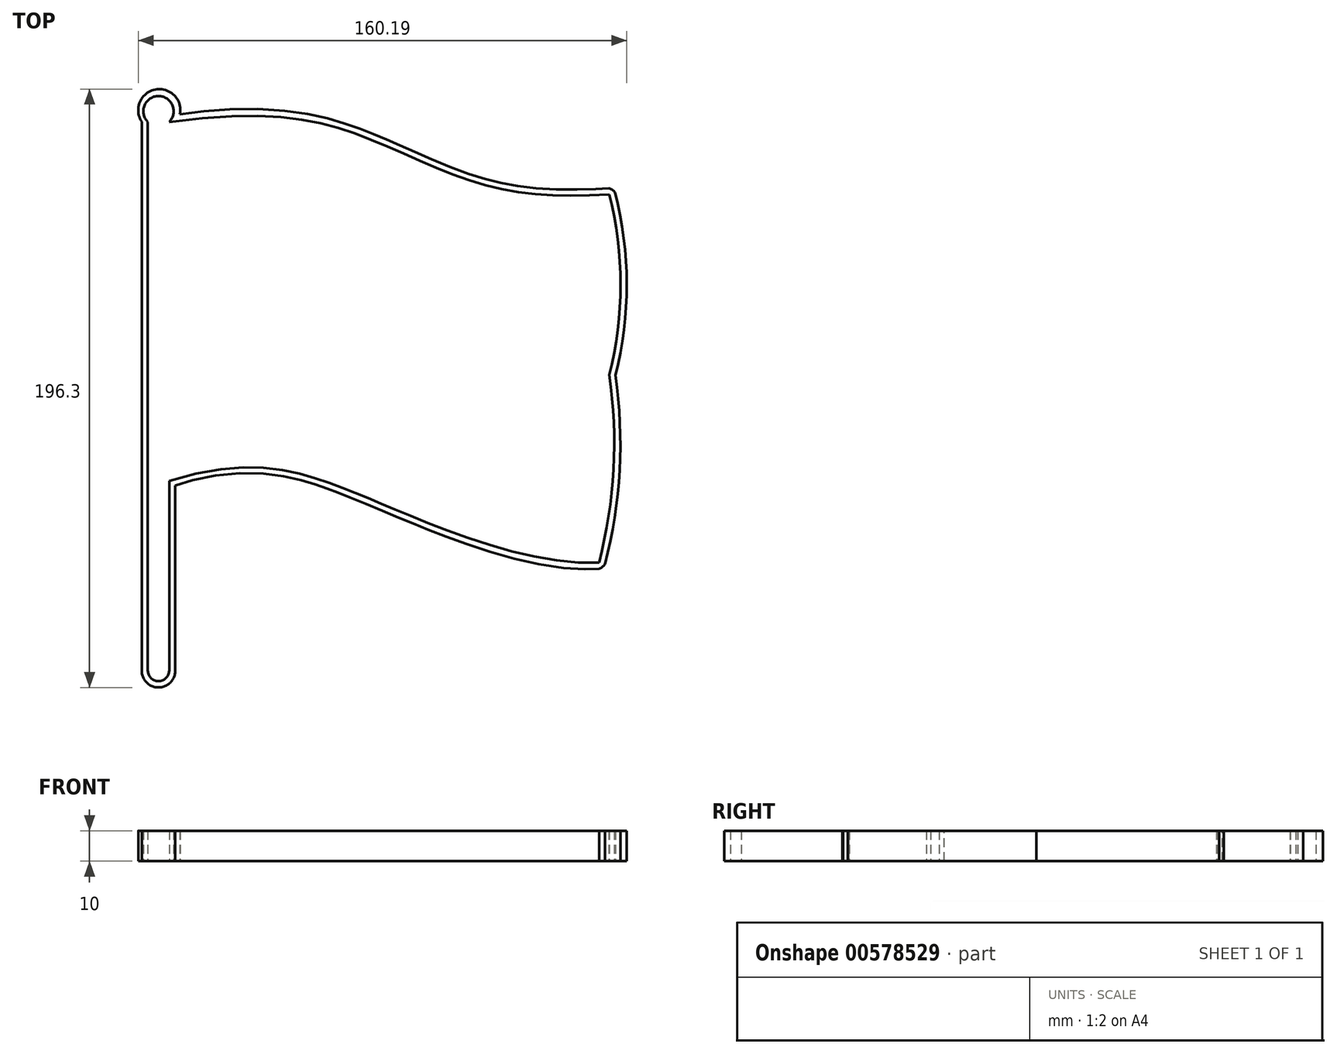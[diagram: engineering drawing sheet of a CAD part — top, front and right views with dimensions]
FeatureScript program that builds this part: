
annotation { "Feature Type Name" : "Feature", "Feature Type Description" : "" }
export const myFeature = defineFeature(function(context is Context, id is Id, definition is map)
    precondition{}
    {
        {
            var Q0;
            Q0=qCreatedBy(makeId("Top.planeOp"),FACE);
            var sketch = newSketch(context, id + "F0", { "sketchPlane" : qUnion([Q0])});
            skLineSegment(sketch, "E0", {"start": v(-42.59, -91.79) * mm, "end": v(-42.59, 88.21) * mm});
            skLineSegment(sketch, "E1.0", {"start": v(-35.59, -91.79) * mm, "end": v(-35.59, 88.21) * mm});
            skCircle(sketch, "E2", {"center": v(-39.09, 91.73) * mm, "radius": 4.96 * mm});
            skPoint(sketch, "E2.third.point", {"position": v(-35.26, 94.9) * mm});
            skArc(sketch, "E3", {"start": v(-42.59, -91.79) * mm, "mid": v(-39.09, -95.29) * mm, "end": v(-35.59, -91.79) * mm});
            skLineSegment(sketch, "E4", {"start": v(-35.59, -91.79) * mm, "end": v(-35.59, -29.6) * mm});
            skFitSpline(sketch, "E5", {"points": [v(-35.59, 88.21) * mm, v(30.46, 82.45) * mm, v(67.82, 67.56) * mm, v(108.72, 64.47) * mm], "startDerivative": vector(265.42, 34.67) * mm, "endDerivative": vector(152.78, 8.66) * mm});
            skFitSpline(sketch, "E6", {"points": [v(-35.59, -29.6) * mm, v(17.53, -30.45) * mm, v(44.5, -41.4) * mm, v(105.38, -56.38) * mm], "startDerivative": vector(212.54, 68.63) * mm, "endDerivative": vector(152.78, 8.66) * mm});
            skArc(sketch, "E7", {"start": v(108.72, 5.18) * mm, "mid": v(112.47, 34.83) * mm, "end": v(108.72, 64.47) * mm});
            skArc(sketch, "E8", {"start": v(105.38, -56.38) * mm, "mid": v(110.14, -25.77) * mm, "end": v(108.72, 5.18) * mm});
            skFitSpline(sketch, "E9.0", {"points": [v(-35.85, 90.2) * mm, v(-24.72, 91.65) * mm, v(-10.89, 92.53) * mm, v(3.7, 91.68) * mm, v(13.16, 90.16) * mm, v(20.18, 88.28) * mm, v(25.5, 86.5) * mm, v(29.38, 85.05) * mm, v(33.23, 83.5) * mm, v(37.08, 81.87) * mm, v(40.93, 80.2) * mm, v(46.05, 77.94) * mm, v(52.44, 75.16) * mm, v(60.07, 72.1) * mm, v(66.39, 70) * mm, v(71.42, 68.67) * mm, v(76.47, 67.59) * mm, v(82.88, 66.64) * mm, v(90.9, 66.1) * mm, v(99.37, 66.04) * mm, v(105.44, 66.3) * mm, v(108.6, 66.47) * mm]});
            skArc(sketch, "E10.0", {"start": v(110.66, 4.7) * mm, "mid": v(114.47, 34.86) * mm, "end": v(110.65, 65) * mm});
            skArc(sketch, "E11.0", {"start": v(107.32, -56.88) * mm, "mid": v(112.14, -25.86) * mm, "end": v(110.7, 5.5) * mm});
            skFitSpline(sketch, "E12.0", {"points": [v(-34.97, -31.51) * mm, v(-30.62, -30.1) * mm, v(-22.51, -28.08) * mm, v(-11.9, -26.95) * mm, v(-2.66, -27.3) * mm, v(4.1, -28.47) * mm, v(9.03, -29.74) * mm, v(12.53, -30.82) * mm, v(15.29, -31.77) * mm, v(17.42, -32.54) * mm, v(19.5, -33.3) * mm, v(22.02, -34.27) * mm, v(25.96, -35.84) * mm, v(30.88, -37.89) * mm, v(36.22, -40.15) * mm, v(41, -42.13) * mm, v(44.89, -43.73) * mm, v(49.13, -45.44) * mm, v(55.2, -47.78) * mm, v(63.4, -50.76) * mm, v(73.88, -54.04) * mm, v(84.64, -56.7) * mm, v(95.34, -58.35) * mm, v(102.2, -58.56) * mm, v(105.5, -58.37) * mm]});
            skLineSegment(sketch, "E13.0", {"start": v(-33.59, -91.83) * mm, "end": v(-33.59, -29.6) * mm});
            skLineSegment(sketch, "E14.0", {"start": v(-44.59, -91.75) * mm, "end": v(-44.59, 88.28) * mm});
            skArc(sketch, "E15", {"start": v(105.5, -58.37) * mm, "mid": v(106.5, -57.76) * mm, "end": v(107.32, -56.88) * mm});
            skArc(sketch, "E16", {"start": v(110.65, 65) * mm, "mid": v(109.76, 65.92) * mm, "end": v(108.6, 66.47) * mm});
            skArc(sketch, "E17", {"start": v(-32.07, 90.67) * mm, "mid": v(-40.12, 98.85) * mm, "end": v(-44.59, 88.28) * mm});
            skArc(sketch, "E18", {"start": v(-44.59, -91.75) * mm, "mid": v(-39.13, -97.33) * mm, "end": v(-33.59, -91.83) * mm});
            skSolve(sketch);
        }
        {
            var Q0;
            {var subQ5=sQuery(id+"F0.wireOp",EDGE,"E0");Q0=makeQuery(id+"F0.imprint","IMPRINT",FACE,{"disambiguationData":[TD([[makeQuery(id+"F0.imprint","IMPRINT",EDGE,{"derivedFrom":subQ5}),1.0]])]});}
            extrude(context, id + "F1", {"entities" : qUnion([Q0]), "depth" : 10 * mm, "offsetDistance" : 25 * mm});
        }
    });
